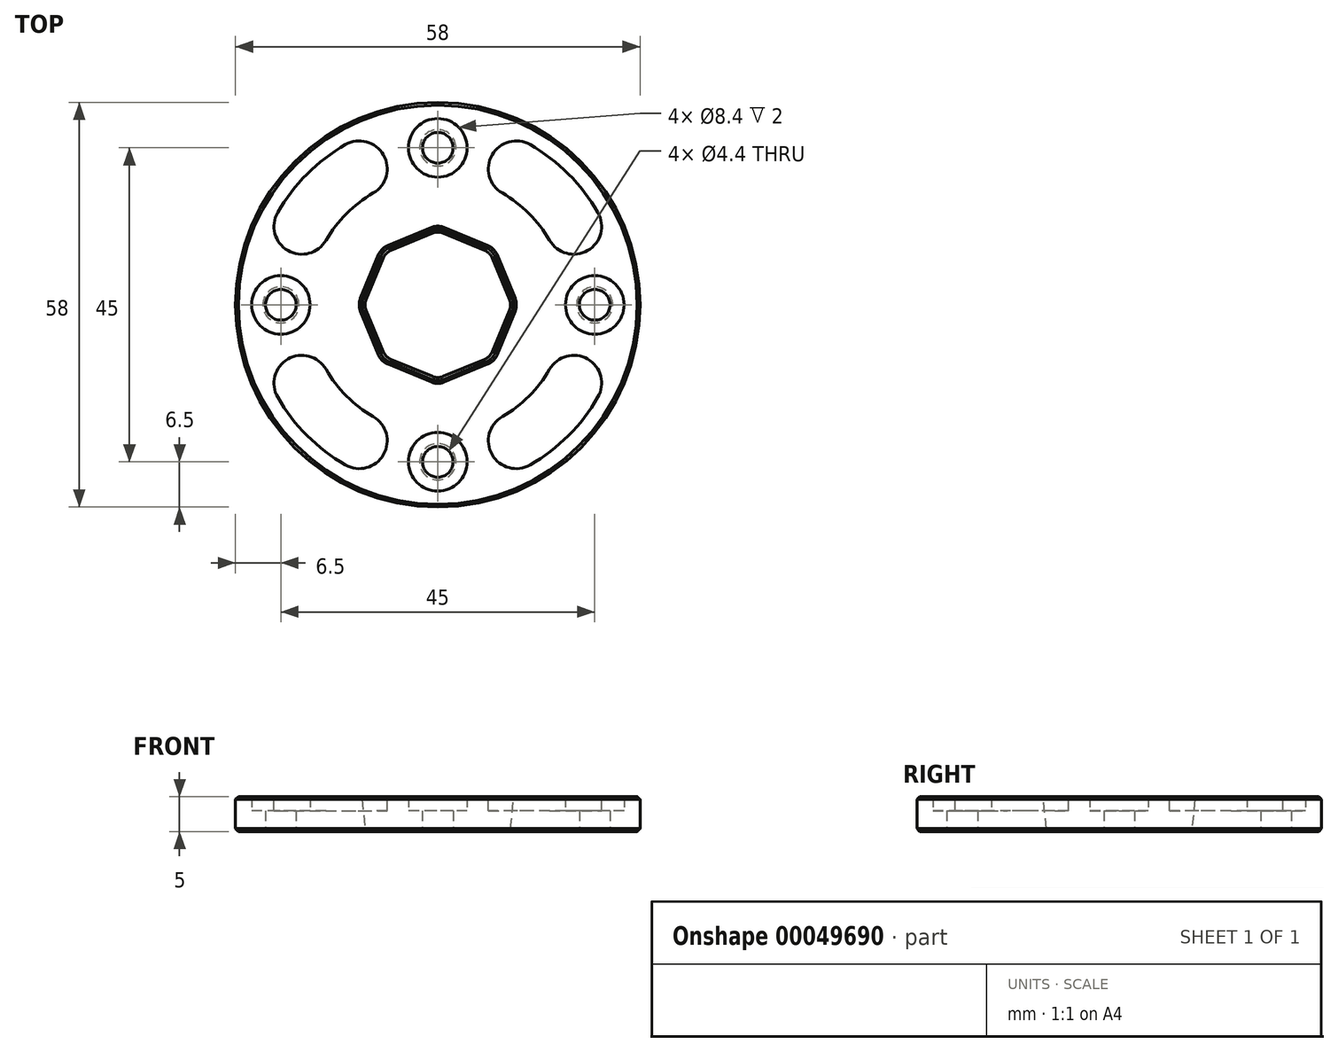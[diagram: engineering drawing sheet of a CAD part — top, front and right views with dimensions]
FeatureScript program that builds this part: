
annotation { "Feature Type Name" : "Feature", "Feature Type Description" : "" }
export const myFeature = defineFeature(function(context is Context, id is Id, definition is map)
    precondition{}
    {
        {
            var Q0;
            Q0=qCreatedBy(makeId("Top.planeOp"),FACE);
            var sketch = newSketch(context, id + "F0", { "sketchPlane" : qUnion([Q0])});
            skCircle(sketch, "E0", {"center": v(0, 0) * mm, "radius": 29 * mm});
            skCircle(sketch, "E1", {"center": v(0, 0) * mm, "radius": 16 * mm});
            skCircle(sketch, "E2.cCircle", {"center": v(0, 0) * mm, "radius": 10.54 * mm, "construction": true});
            skLineSegment(sketch, "E2.0", {"start": v(0, 10.54) * mm, "end": v(7.45, 7.45) * mm});
            skLineSegment(sketch, "E2.1", {"start": v(7.45, 7.45) * mm, "end": v(10.54, 0) * mm});
            skLineSegment(sketch, "E2.2", {"start": v(10.54, 0) * mm, "end": v(7.45, -7.45) * mm});
            skLineSegment(sketch, "E2.3", {"start": v(7.45, -7.45) * mm, "end": v(0, -10.54) * mm});
            skLineSegment(sketch, "E2.4", {"start": v(0, -10.54) * mm, "end": v(-7.45, -7.45) * mm});
            skLineSegment(sketch, "E2.5", {"start": v(-7.45, -7.45) * mm, "end": v(-10.54, 0) * mm});
            skLineSegment(sketch, "E2.6", {"start": v(-10.54, 0) * mm, "end": v(-7.45, 7.45) * mm});
            skLineSegment(sketch, "E2.7", {"start": v(-7.45, 7.45) * mm, "end": v(0, 10.54) * mm});
            skLineSegment(sketch, "E3", {"start": v(0, 29) * mm, "end": v(0, 16) * mm, "construction": true});
            skCircle(sketch, "E4", {"center": v(0, 22.5) * mm, "radius": 4.2 * mm});
            skCircle(sketch, "E5", {"center": v(0, 22.5) * mm, "radius": 2.2 * mm});
            skLineSegment(sketch, "E6", {"start": v(16, 0) * mm, "end": v(29, 0) * mm, "construction": true});
            skLineSegment(sketch, "E7", {"start": v(0, -16) * mm, "end": v(0, -29) * mm, "construction": true});
            skLineSegment(sketch, "E8", {"start": v(-16, 0) * mm, "end": v(-29, 0) * mm, "construction": true});
            skCircle(sketch, "E9", {"center": v(-22.5, 0) * mm, "radius": 4.2 * mm});
            skCircle(sketch, "E10", {"center": v(-22.5, 0) * mm, "radius": 2.2 * mm});
            skCircle(sketch, "E11", {"center": v(0, -22.5) * mm, "radius": 4.2 * mm});
            skCircle(sketch, "E12", {"center": v(0, -22.5) * mm, "radius": 2.2 * mm});
            skCircle(sketch, "E13", {"center": v(22.5, 0) * mm, "radius": 4.2 * mm});
            skCircle(sketch, "E14", {"center": v(22.5, 0) * mm, "radius": 2.2 * mm});
            skLineSegment(sketch, "E15", {"start": v(0, 0) * mm, "end": v(3.5, 0) * mm, "construction": true});
            skCircle(sketch, "E16", {"center": v(3.5, 0) * mm, "radius": 6.5 * mm, "construction": true});
            skPoint(sketch, "E17", {"position": v(10, 0) * mm});
            skSolve(sketch);
        }
        {
            var Q0;
            Q0=makeQuery(id+"F0.imprint","IMPRINT",FACE,{"disambiguationData":[TD([[makeQuery(id+"F0.imprint","IMPRINT",EDGE,{"derivedFrom":sQuery(id+"F0.wireOp",EDGE,"E0")}),1.0]])]});
            var Q1;
            Q1=makeQuery(id+"F0.imprint","IMPRINT",FACE,{"disambiguationData":[TD([[makeQuery(id+"F0.imprint","IMPRINT",EDGE,{"derivedFrom":sQuery(id+"F0.wireOp",EDGE,"E1")}),1.0]])]});
            extrude(context, id + "F7", {"entities" : qUnion([Q0, Q1]), "depth" : 5 * mm});
        }
        {
            var Q0;
            Q0=makeQuery(id+"F0.imprint","IMPRINT",FACE,{"disambiguationData":[TD([[makeQuery(id+"F0.imprint","IMPRINT",EDGE,{"derivedFrom":sQuery(id+"F0.wireOp",EDGE,"E4")}),1.0]])]});
            var Q1;
            Q1=makeQuery(id+"F0.imprint","IMPRINT",FACE,{"disambiguationData":[TD([[makeQuery(id+"F0.imprint","IMPRINT",EDGE,{"derivedFrom":sQuery(id+"F0.wireOp",EDGE,"E9")}),1.0]])]});
            var Q2;
            Q2=makeQuery(id+"F0.imprint","IMPRINT",FACE,{"disambiguationData":[TD([[makeQuery(id+"F0.imprint","IMPRINT",EDGE,{"derivedFrom":sQuery(id+"F0.wireOp",EDGE,"E11")}),1.0]])]});
            var Q3;
            Q3=makeQuery(id+"F0.imprint","IMPRINT",FACE,{"disambiguationData":[TD([[makeQuery(id+"F0.imprint","IMPRINT",EDGE,{"derivedFrom":sQuery(id+"F0.wireOp",EDGE,"E13")}),1.0]])]});
            extrude(context, id + "F1", {"entities" : qUnion([Q0, Q1, Q2, Q3]), "operationType" : NewBodyOperationType.ADD, "depth" : 3 * mm});
        }
        {
            var Q0;
            Q0=makeQuery(id+"F7.opExtrude","CAP_EDGE",EDGE,{"disambiguationData":[OSD([sQuery(id+"F0.wireOp",EDGE,"E2.6")])],"isStart":false});
            var Q1;
            Q1=makeQuery(id+"F7.opExtrude","CAP_EDGE",EDGE,{"disambiguationData":[OSD([sQuery(id+"F0.wireOp",EDGE,"E2.7")])],"isStart":false});
            var Q2;
            Q2=makeQuery(id+"F7.opExtrude","CAP_EDGE",EDGE,{"disambiguationData":[OSD([sQuery(id+"F0.wireOp",EDGE,"E2.0")])],"isStart":false});
            var Q3;
            Q3=makeQuery(id+"F7.opExtrude","CAP_EDGE",EDGE,{"disambiguationData":[OSD([sQuery(id+"F0.wireOp",EDGE,"E2.1")])],"isStart":false});
            var Q4;
            Q4=makeQuery(id+"F7.opExtrude","CAP_EDGE",EDGE,{"disambiguationData":[OSD([sQuery(id+"F0.wireOp",EDGE,"E2.2")])],"isStart":false});
            var Q5;
            Q5=makeQuery(id+"F7.opExtrude","CAP_EDGE",EDGE,{"disambiguationData":[OSD([sQuery(id+"F0.wireOp",EDGE,"E2.3")])],"isStart":false});
            var Q6;
            Q6=makeQuery(id+"F7.opExtrude","CAP_EDGE",EDGE,{"disambiguationData":[OSD([sQuery(id+"F0.wireOp",EDGE,"E2.4")])],"isStart":false});
            var Q7;
            Q7=makeQuery(id+"F7.opExtrude","CAP_EDGE",EDGE,{"disambiguationData":[OSD([sQuery(id+"F0.wireOp",EDGE,"E2.5")])],"isStart":false});
            chamfer(context, id + "F2", {"entities" : qUnion([Q0, Q1, Q2, Q3, Q4, Q5, Q6, Q7]), "chamferType" : ChamferType.TWO_OFFSETS, "width1" : .5 * mm, "oppositeDirection" : false, "width2" : 5 * mm, "tangentPropagation" : true});
        }
        {
            var Q0;
            Q0=makeQuery(id+"F2.opChamfer","BLEND_EDGE",EDGE,{"blendedFrom":[makeQuery(id+"F7.opExtrude","CAP_EDGE",EDGE,{"disambiguationData":[OSD([sQuery(id+"F0.wireOp",EDGE,"E2.0")])],"isStart":false}),makeQuery(id+"F7.opExtrude","CAP_EDGE",EDGE,{"disambiguationData":[OSD([sQuery(id+"F0.wireOp",EDGE,"E2.7")])],"isStart":false})],"blendedInto":[]});
            var Q1;
            Q1=makeQuery(id+"F2.opChamfer","BLEND_EDGE",EDGE,{"blendedFrom":[makeQuery(id+"F7.opExtrude","CAP_EDGE",EDGE,{"disambiguationData":[OSD([sQuery(id+"F0.wireOp",EDGE,"E2.0")])],"isStart":false}),makeQuery(id+"F7.opExtrude","CAP_EDGE",EDGE,{"disambiguationData":[OSD([sQuery(id+"F0.wireOp",EDGE,"E2.1")])],"isStart":false})],"blendedInto":[]});
            var Q2;
            Q2=makeQuery(id+"F2.opChamfer","BLEND_EDGE",EDGE,{"blendedFrom":[makeQuery(id+"F7.opExtrude","CAP_EDGE",EDGE,{"disambiguationData":[OSD([sQuery(id+"F0.wireOp",EDGE,"E2.1")])],"isStart":false}),makeQuery(id+"F7.opExtrude","CAP_EDGE",EDGE,{"disambiguationData":[OSD([sQuery(id+"F0.wireOp",EDGE,"E2.2")])],"isStart":false})],"blendedInto":[]});
            var Q3;
            Q3=makeQuery(id+"F2.opChamfer","BLEND_EDGE",EDGE,{"blendedFrom":[makeQuery(id+"F7.opExtrude","CAP_EDGE",EDGE,{"disambiguationData":[OSD([sQuery(id+"F0.wireOp",EDGE,"E2.2")])],"isStart":false}),makeQuery(id+"F7.opExtrude","CAP_EDGE",EDGE,{"disambiguationData":[OSD([sQuery(id+"F0.wireOp",EDGE,"E2.3")])],"isStart":false})],"blendedInto":[]});
            var Q4;
            Q4=makeQuery(id+"F2.opChamfer","BLEND_EDGE",EDGE,{"blendedFrom":[makeQuery(id+"F7.opExtrude","CAP_EDGE",EDGE,{"disambiguationData":[OSD([sQuery(id+"F0.wireOp",EDGE,"E2.3")])],"isStart":false}),makeQuery(id+"F7.opExtrude","CAP_EDGE",EDGE,{"disambiguationData":[OSD([sQuery(id+"F0.wireOp",EDGE,"E2.4")])],"isStart":false})],"blendedInto":[]});
            var Q5;
            Q5=makeQuery(id+"F2.opChamfer","BLEND_EDGE",EDGE,{"blendedFrom":[makeQuery(id+"F7.opExtrude","CAP_EDGE",EDGE,{"disambiguationData":[OSD([sQuery(id+"F0.wireOp",EDGE,"E2.4")])],"isStart":false}),makeQuery(id+"F7.opExtrude","CAP_EDGE",EDGE,{"disambiguationData":[OSD([sQuery(id+"F0.wireOp",EDGE,"E2.5")])],"isStart":false})],"blendedInto":[]});
            var Q6;
            Q6=makeQuery(id+"F2.opChamfer","BLEND_EDGE",EDGE,{"blendedFrom":[makeQuery(id+"F7.opExtrude","CAP_EDGE",EDGE,{"disambiguationData":[OSD([sQuery(id+"F0.wireOp",EDGE,"E2.5")])],"isStart":false}),makeQuery(id+"F7.opExtrude","CAP_EDGE",EDGE,{"disambiguationData":[OSD([sQuery(id+"F0.wireOp",EDGE,"E2.6")])],"isStart":false})],"blendedInto":[]});
            var Q7;
            Q7=makeQuery(id+"F2.opChamfer","BLEND_EDGE",EDGE,{"blendedFrom":[makeQuery(id+"F7.opExtrude","CAP_EDGE",EDGE,{"disambiguationData":[OSD([sQuery(id+"F0.wireOp",EDGE,"E2.6")])],"isStart":false}),makeQuery(id+"F7.opExtrude","CAP_EDGE",EDGE,{"disambiguationData":[OSD([sQuery(id+"F0.wireOp",EDGE,"E2.7")])],"isStart":false})],"blendedInto":[]});
            fillet(context, id + "F3", {"entities" : qUnion([Q0, Q1, Q2, Q3, Q4, Q5, Q6, Q7]), "radius" : 2 * mm, "tangentPropagation" : true, "allowEdgeOverflow" : false});
        }
        {
            var Q0;
            Q0=makeQuery(id+"F7.opExtrude","CAP_FACE",FACE,{"disambiguationData":[OSD([sQuery(id+"F0.wireOp",EDGE,"E0"),sQuery(id+"F0.wireOp",EDGE,"E2.0"),sQuery(id+"F0.wireOp",EDGE,"E2.1"),sQuery(id+"F0.wireOp",EDGE,"E2.2"),sQuery(id+"F0.wireOp",EDGE,"E2.3"),sQuery(id+"F0.wireOp",EDGE,"E2.4"),sQuery(id+"F0.wireOp",EDGE,"E2.5"),sQuery(id+"F0.wireOp",EDGE,"E2.6"),sQuery(id+"F0.wireOp",EDGE,"E2.7"),sQuery(id+"F0.wireOp",EDGE,"E4"),sQuery(id+"F0.wireOp",EDGE,"E9"),sQuery(id+"F0.wireOp",EDGE,"E11"),sQuery(id+"F0.wireOp",EDGE,"E13")])],"isStart":false});
            var sketch = newSketch(context, id + "F4", { "sketchPlane" : qUnion([Q0])});
            skCircle(sketch, "E18", {"center": v(0, 0) * mm, "radius": 22.5 * mm, "construction": true});
            skCircle(sketch, "E19.0", {"center": v(-22.5, 0) * mm, "radius": 2.2 * mm, "construction": true});
            skArc(sketch, "E20", {"start": v(-22.95, 13.25) * mm, "mid": v(-21.49, 7.79) * mm, "end": v(-16.02, 9.25) * mm});
            skArc(sketch, "E21", {"start": v(-9.25, 16.02) * mm, "mid": v(-7.79, 21.49) * mm, "end": v(-13.25, 22.95) * mm});
            skLineSegment(sketch, "E22", {"start": v(-11.25, 19.49) * mm, "end": v(0, 0) * mm, "construction": true});
            skLineSegment(sketch, "E23", {"start": v(-19.49, 11.25) * mm, "end": v(0, 0) * mm, "construction": true});
            skLineSegment(sketch, "E24", {"start": v(-22.5, 0) * mm, "end": v(0, 0) * mm, "construction": true});
            skLineSegment(sketch, "E25", {"start": v(0, 22.5) * mm, "end": v(0, 0) * mm, "construction": true});
            skArc(sketch, "E26", {"start": v(-13.25, 22.95) * mm, "mid": v(-18.74, 18.74) * mm, "end": v(-22.95, 13.25) * mm});
            skArc(sketch, "E27", {"start": v(-9.25, 16.02) * mm, "mid": v(-13.08, 13.08) * mm, "end": v(-16.02, 9.25) * mm});
            skArc(sketch, "E28.1.0", {"start": v(-16.02, -9.25) * mm, "mid": v(-13.08, -13.08) * mm, "end": v(-9.25, -16.02) * mm});
            skArc(sketch, "E28.1.1", {"start": v(-16.02, -9.25) * mm, "mid": v(-21.49, -7.79) * mm, "end": v(-22.95, -13.25) * mm});
            skArc(sketch, "E28.1.2", {"start": v(-22.95, -13.25) * mm, "mid": v(-18.74, -18.74) * mm, "end": v(-13.25, -22.95) * mm});
            skArc(sketch, "E28.1.3", {"start": v(-13.25, -22.95) * mm, "mid": v(-7.79, -21.49) * mm, "end": v(-9.25, -16.02) * mm});
            skArc(sketch, "E28.2.0", {"start": v(9.25, -16.02) * mm, "mid": v(13.08, -13.08) * mm, "end": v(16.02, -9.25) * mm});
            skArc(sketch, "E28.2.1", {"start": v(9.25, -16.02) * mm, "mid": v(7.79, -21.49) * mm, "end": v(13.25, -22.95) * mm});
            skArc(sketch, "E28.2.2", {"start": v(13.25, -22.95) * mm, "mid": v(18.74, -18.74) * mm, "end": v(22.95, -13.25) * mm});
            skArc(sketch, "E28.2.3", {"start": v(22.95, -13.25) * mm, "mid": v(21.49, -7.79) * mm, "end": v(16.02, -9.25) * mm});
            skArc(sketch, "E29.0.3.0", {"start": v(16.02, 9.25) * mm, "mid": v(13.08, 13.08) * mm, "end": v(9.25, 16.02) * mm});
            skArc(sketch, "E29.4.3.0", {"start": v(16.02, 9.25) * mm, "mid": v(21.49, 7.79) * mm, "end": v(22.95, 13.25) * mm});
            skArc(sketch, "E29.8.3.0", {"start": v(22.95, 13.25) * mm, "mid": v(18.74, 18.74) * mm, "end": v(13.25, 22.95) * mm});
            skArc(sketch, "E29.12.3.0", {"start": v(13.25, 22.95) * mm, "mid": v(7.79, 21.49) * mm, "end": v(9.25, 16.02) * mm});
            skSolve(sketch);
        }
        {
            var Q0;
            Q0=makeQuery(id+"F4.imprint","IMPRINT",FACE,{"disambiguationData":[TD([[makeQuery(id+"F4.imprint","IMPRINT",EDGE,{"derivedFrom":sQuery(id+"F4.wireOp",EDGE,"E28.1.0")}),-1.0]])]});
            var Q1;
            Q1=makeQuery(id+"F4.imprint","IMPRINT",FACE,{"disambiguationData":[TD([[makeQuery(id+"F4.imprint","IMPRINT",EDGE,{"derivedFrom":sQuery(id+"F4.wireOp",EDGE,"E20")}),1.0]])]});
            var Q2;
            Q2=makeQuery(id+"F4.imprint","IMPRINT",FACE,{"disambiguationData":[TD([[makeQuery(id+"F4.imprint","IMPRINT",EDGE,{"derivedFrom":sQuery(id+"F4.wireOp",EDGE,"E29.0.3.0")}),-1.0]])]});
            var Q3;
            Q3=makeQuery(id+"F4.imprint","IMPRINT",FACE,{"disambiguationData":[TD([[makeQuery(id+"F4.imprint","IMPRINT",EDGE,{"derivedFrom":sQuery(id+"F4.wireOp",EDGE,"E28.2.0")}),-1.0]])]});
            extrude(context, id + "F5", {"entities" : qUnion([Q0, Q1, Q2, Q3]), "operationType" : NewBodyOperationType.REMOVE, "oppositeDirection" : true, "depth" : 2 * mm});
        }
        {
            var Q0;
            Q0=makeQuery(id+"F7.opExtrude","CAP_EDGE",EDGE,{"disambiguationData":[OSD([sQuery(id+"F0.wireOp",EDGE,"E0")])],"isStart":true});
            var Q1;
            Q1=makeQuery(id+"F1.opExtrude","CAP_EDGE",EDGE,{"disambiguationData":[OSD([sQuery(id+"F0.wireOp",EDGE,"E10")])],"isStart":true});
            var Q2;
            Q2=makeQuery(id+"F1.opExtrude","CAP_EDGE",EDGE,{"disambiguationData":[OSD([sQuery(id+"F0.wireOp",EDGE,"E12")])],"isStart":true});
            var Q3;
            Q3=makeQuery(id+"F1.opExtrude","CAP_EDGE",EDGE,{"disambiguationData":[OSD([sQuery(id+"F0.wireOp",EDGE,"E14")])],"isStart":true});
            var Q4;
            Q4=makeQuery(id+"F1.opExtrude","CAP_EDGE",EDGE,{"disambiguationData":[OSD([sQuery(id+"F0.wireOp",EDGE,"E5")])],"isStart":true});
            var Q5;
            Q5=makeQuery(id+"F7.opExtrude","CAP_EDGE",EDGE,{"disambiguationData":[OSD([sQuery(id+"F0.wireOp",EDGE,"E0")])],"isStart":false});
            var Q6;
            {var subQ0=sQuery(id+"F0.wireOp",EDGE,"E2.6");Q6=makeQuery(id+"F2.opChamfer","BLEND_EDGE",EDGE,{"blendedFrom":[makeQuery(id+"F7.opExtrude","CAP_EDGE",EDGE,{"disambiguationData":[OSD([subQ0])],"isStart":false}),makeQuery(id+"F7.opExtrude","CAP_FACE",FACE,{"disambiguationData":[OSD([sQuery(id+"F0.wireOp",EDGE,"E0"),sQuery(id+"F0.wireOp",EDGE,"E2.0"),sQuery(id+"F0.wireOp",EDGE,"E2.1"),sQuery(id+"F0.wireOp",EDGE,"E2.2"),sQuery(id+"F0.wireOp",EDGE,"E2.3"),sQuery(id+"F0.wireOp",EDGE,"E2.4"),sQuery(id+"F0.wireOp",EDGE,"E2.5"),subQ0,sQuery(id+"F0.wireOp",EDGE,"E2.7"),sQuery(id+"F0.wireOp",EDGE,"E4"),sQuery(id+"F0.wireOp",EDGE,"E9"),sQuery(id+"F0.wireOp",EDGE,"E11"),sQuery(id+"F0.wireOp",EDGE,"E13")])],"isStart":false})],"blendedInto":[makeQuery(id+"F7.opExtrude","CAP_FACE",FACE,{"disambiguationData":[OSD([sQuery(id+"F0.wireOp",EDGE,"E0"),sQuery(id+"F0.wireOp",EDGE,"E2.0"),sQuery(id+"F0.wireOp",EDGE,"E2.1"),sQuery(id+"F0.wireOp",EDGE,"E2.2"),sQuery(id+"F0.wireOp",EDGE,"E2.3"),sQuery(id+"F0.wireOp",EDGE,"E2.4"),sQuery(id+"F0.wireOp",EDGE,"E2.5"),subQ0,sQuery(id+"F0.wireOp",EDGE,"E2.7"),sQuery(id+"F0.wireOp",EDGE,"E4"),sQuery(id+"F0.wireOp",EDGE,"E9"),sQuery(id+"F0.wireOp",EDGE,"E11"),sQuery(id+"F0.wireOp",EDGE,"E13")])],"isStart":false})]});}
            var Q7;
            {var subQ0=sQuery(id+"F0.wireOp",EDGE,"E2.6");var subQ1=sQuery(id+"F0.wireOp",EDGE,"E4");var subQ2=sQuery(id+"F0.wireOp",EDGE,"E9");var subQ3=sQuery(id+"F0.wireOp",EDGE,"E11");var subQ4=sQuery(id+"F0.wireOp",EDGE,"E13");Q7=makeQuery(id+"F2.opChamfer","BLEND_EDGE",EDGE,{"blendedFrom":[makeQuery(id+"F7.opExtrude","CAP_EDGE",EDGE,{"disambiguationData":[OSD([subQ0])],"isStart":false}),makeQuery(id+"F1.boolean.opBoolean","MERGE",FACE,{"derivedFrom":[makeQuery(id+"F7.opExtrude","CAP_FACE",FACE,{"disambiguationData":[OSD([sQuery(id+"F0.wireOp",EDGE,"E0"),sQuery(id+"F0.wireOp",EDGE,"E2.0"),sQuery(id+"F0.wireOp",EDGE,"E2.1"),sQuery(id+"F0.wireOp",EDGE,"E2.2"),sQuery(id+"F0.wireOp",EDGE,"E2.3"),sQuery(id+"F0.wireOp",EDGE,"E2.4"),sQuery(id+"F0.wireOp",EDGE,"E2.5"),subQ0,sQuery(id+"F0.wireOp",EDGE,"E2.7"),subQ1,subQ2,subQ3,subQ4])],"isStart":true}),makeQuery(id+"F1.opExtrude","CAP_FACE",FACE,{"disambiguationData":[OSD([subQ1,sQuery(id+"F0.wireOp",EDGE,"E5")])],"isStart":true}),makeQuery(id+"F1.opExtrude","CAP_FACE",FACE,{"disambiguationData":[OSD([subQ2,sQuery(id+"F0.wireOp",EDGE,"E10")])],"isStart":true}),makeQuery(id+"F1.opExtrude","CAP_FACE",FACE,{"disambiguationData":[OSD([subQ3,sQuery(id+"F0.wireOp",EDGE,"E12")])],"isStart":true}),makeQuery(id+"F1.opExtrude","CAP_FACE",FACE,{"disambiguationData":[OSD([subQ4,sQuery(id+"F0.wireOp",EDGE,"E14")])],"isStart":true})]})],"blendedInto":[makeQuery(id+"F1.boolean.opBoolean","MERGE",FACE,{"derivedFrom":[makeQuery(id+"F7.opExtrude","CAP_FACE",FACE,{"disambiguationData":[OSD([sQuery(id+"F0.wireOp",EDGE,"E0"),sQuery(id+"F0.wireOp",EDGE,"E2.0"),sQuery(id+"F0.wireOp",EDGE,"E2.1"),sQuery(id+"F0.wireOp",EDGE,"E2.2"),sQuery(id+"F0.wireOp",EDGE,"E2.3"),sQuery(id+"F0.wireOp",EDGE,"E2.4"),sQuery(id+"F0.wireOp",EDGE,"E2.5"),subQ0,sQuery(id+"F0.wireOp",EDGE,"E2.7"),subQ1,subQ2,subQ3,subQ4])],"isStart":true}),makeQuery(id+"F1.opExtrude","CAP_FACE",FACE,{"disambiguationData":[OSD([subQ1,sQuery(id+"F0.wireOp",EDGE,"E5")])],"isStart":true}),makeQuery(id+"F1.opExtrude","CAP_FACE",FACE,{"disambiguationData":[OSD([subQ2,sQuery(id+"F0.wireOp",EDGE,"E10")])],"isStart":true}),makeQuery(id+"F1.opExtrude","CAP_FACE",FACE,{"disambiguationData":[OSD([subQ3,sQuery(id+"F0.wireOp",EDGE,"E12")])],"isStart":true}),makeQuery(id+"F1.opExtrude","CAP_FACE",FACE,{"disambiguationData":[OSD([subQ4,sQuery(id+"F0.wireOp",EDGE,"E14")])],"isStart":true})]})]});}
            chamfer(context, id + "F6", {"entities" : qUnion([Q0, Q1, Q2, Q3, Q4, Q5, Q6, Q7]), "width" : .4 * mm, "tangentPropagation" : true});
        }
    });
